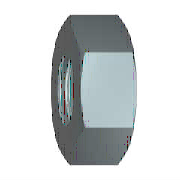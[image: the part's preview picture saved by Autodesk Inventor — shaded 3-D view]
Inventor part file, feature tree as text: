
AUTODESK INVENTOR PART (.ipt)
format: ipt  version: 2017 (Build 210142000, 142)  size: 173,568 bytes
history: native  units: mm (DEFAULTED — no unit token found)
features: sketch x3, chamfer x1, hole x1, other x1, plane x1
ambient origin geometry x7: Origin, YZ Plane, XZ Plane, X Axis, Y Axis, Z Axis, Center Point
bodies: Solid1 (feature_tree), Body (feature_tree)
feature tree (7):
  chamfer  "Chamfer1"  Distance=4.363323mm
  hole  "Thread"  [1 undecoded]
  other  "Work Axis1"
  plane  "Work Plane1"
  sketch  "Sketch1"  dims[d0=8.082904mm]
  sketch  "Sketch2"  dims[d1=3.2mm]
  sketch  "Sketch3"  dims[d2=0.0mm d3=4.363323mm d4=4.363323mm d5=7.0mm d6=7.0mm d7=90.0deg d25=3.242mm d26=6.0mm d27=4.0mm d28=2.0mm d29=14.3117mm d30=8.0mm d31=20.594885mm d8=0.378886mm d9=30.0deg d10=0.378886mm d11=30.0deg d13=0.0mm d14=0.0mm d39=0.0mm d40=0.378886mm d41=0.378886mm d42=0.0mm]
note: 1 required parameter value undecoded (feature->parameter linkage not recoverable at this tier; creation-order binding heuristic only, values carry confidence <= 0.55)
